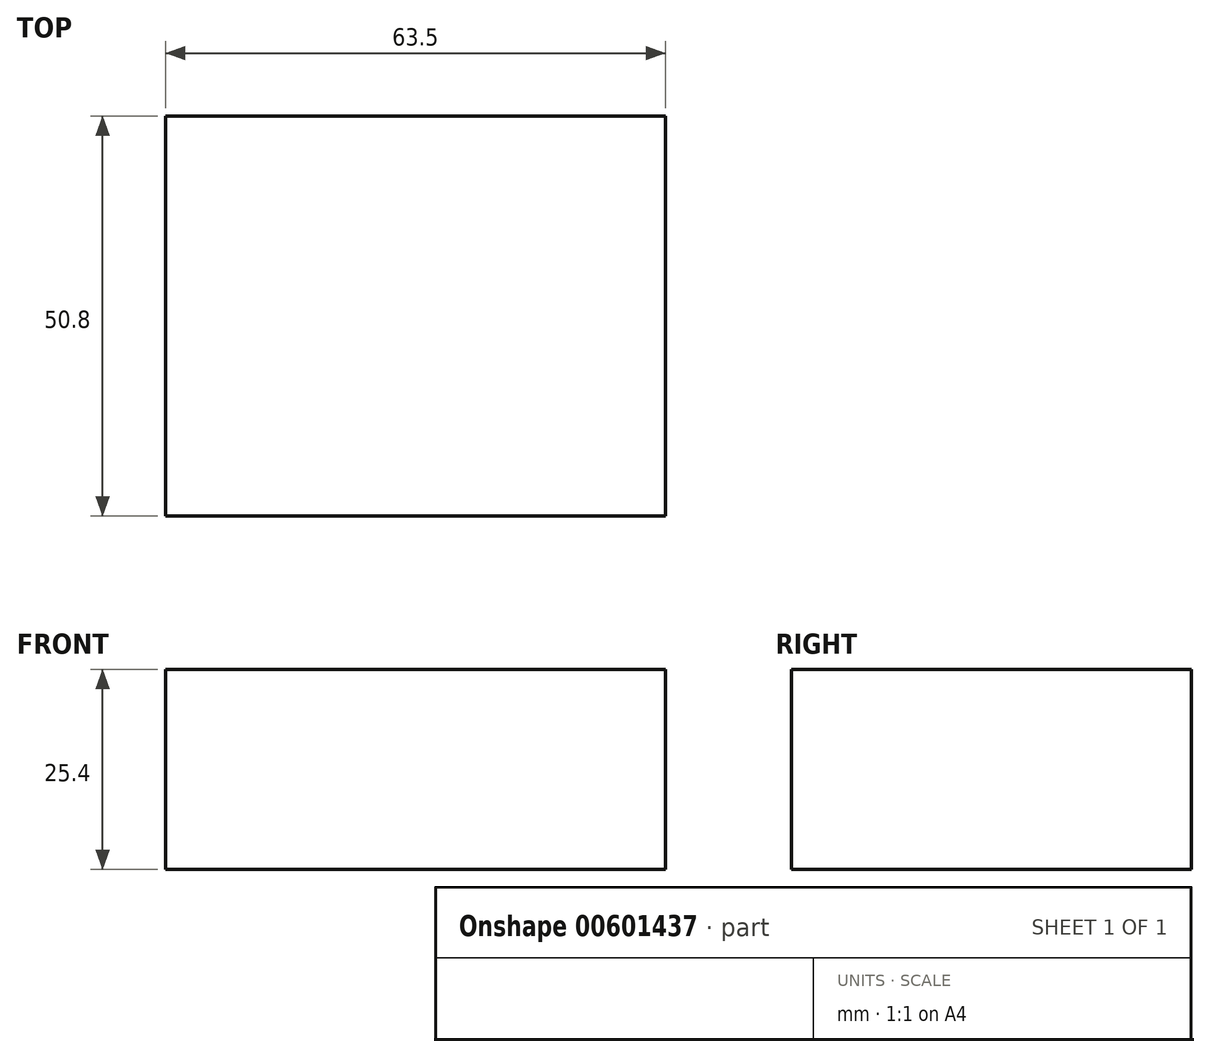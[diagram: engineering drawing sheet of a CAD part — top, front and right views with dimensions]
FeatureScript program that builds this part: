
annotation { "Feature Type Name" : "Feature", "Feature Type Description" : "" }
export const myFeature = defineFeature(function(context is Context, id is Id, definition is map)
    precondition{}
    {
        {
            var Q0;
            Q0=qCreatedBy(makeId("Top.planeOp"),FACE);
            var sketch = newSketch(context, id + "F0", { "sketchPlane" : qUnion([Q0])});
            skLineSegment(sketch, "E0.bottom", {"start": v(0, 0) * mm, "end": v(63.5, 0) * mm});
            skLineSegment(sketch, "E0.top", {"start": v(0, 50.8) * mm, "end": v(63.5, 50.8) * mm});
            skLineSegment(sketch, "E0.left", {"start": v(0, 0) * mm, "end": v(0, 50.8) * mm});
            skLineSegment(sketch, "E0.right", {"start": v(63.5, 0) * mm, "end": v(63.5, 50.8) * mm});
            skSolve(sketch);
        }
        {
            var Q0;
            Q0=makeQuery(id+"F0.imprint","IMPRINT",FACE,{"disambiguationData":[TD([[makeQuery(id+"F0.imprint","IMPRINT",EDGE,{"derivedFrom":sQuery(id+"F0.wireOp",EDGE,"E0.bottom")}),1.0]])]});
            extrude(context, id + "F1", {"entities" : qUnion([Q0]), "depth" : 25.4 * mm, "offsetDistance" : 25.4 * mm});
        }
    });
